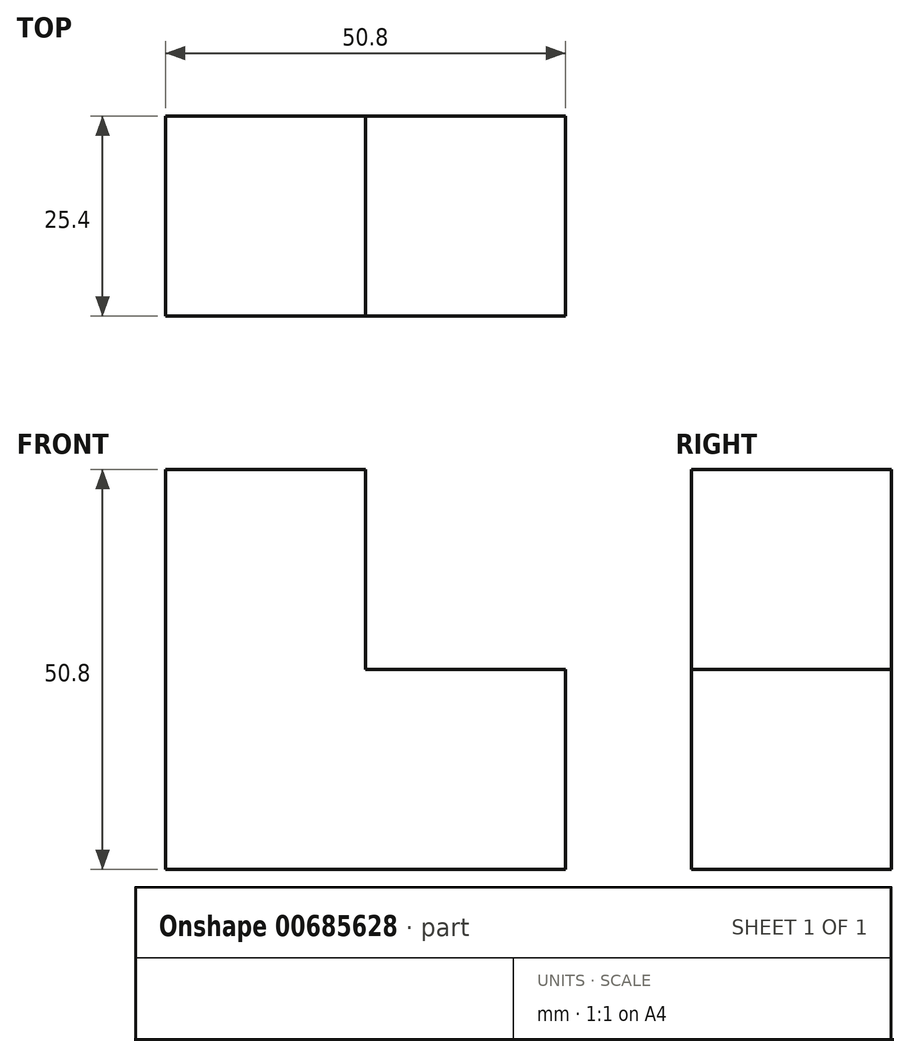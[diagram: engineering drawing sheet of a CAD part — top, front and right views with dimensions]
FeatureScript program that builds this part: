
annotation { "Feature Type Name" : "Feature", "Feature Type Description" : "" }
export const myFeature = defineFeature(function(context is Context, id is Id, definition is map)
    precondition{}
    {
        {
            var Q0;
            Q0=qCreatedBy(makeId("Front.planeOp"),FACE);
            var sketch = newSketch(context, id + "F0", { "sketchPlane" : qUnion([Q0])});
            skLineSegment(sketch, "E0", {"start": v(-45.62, 52.42) * mm, "end": v(-45.62, 1.62) * mm});
            skLineSegment(sketch, "E1", {"start": v(-45.62, 1.62) * mm, "end": v(5.18, 1.62) * mm});
            skLineSegment(sketch, "E2", {"start": v(-45.62, 52.42) * mm, "end": v(-20.22, 52.42) * mm});
            skLineSegment(sketch, "E3", {"start": v(-20.22, 52.42) * mm, "end": v(-20.22, 27.02) * mm});
            skLineSegment(sketch, "E4", {"start": v(-20.22, 27.02) * mm, "end": v(5.18, 27.02) * mm});
            skLineSegment(sketch, "E5", {"start": v(5.18, 27.02) * mm, "end": v(5.18, 1.62) * mm});
            skSolve(sketch);
        }
        {
            var Q0;
            Q0 = qSketchRegion(id + "F0", true);
            extrude(context, id + "F1", {"entities" : qUnion([Q0]), "depth" : 25.4 * mm, "offsetDistance" : 25.4 * mm});
        }
    });
